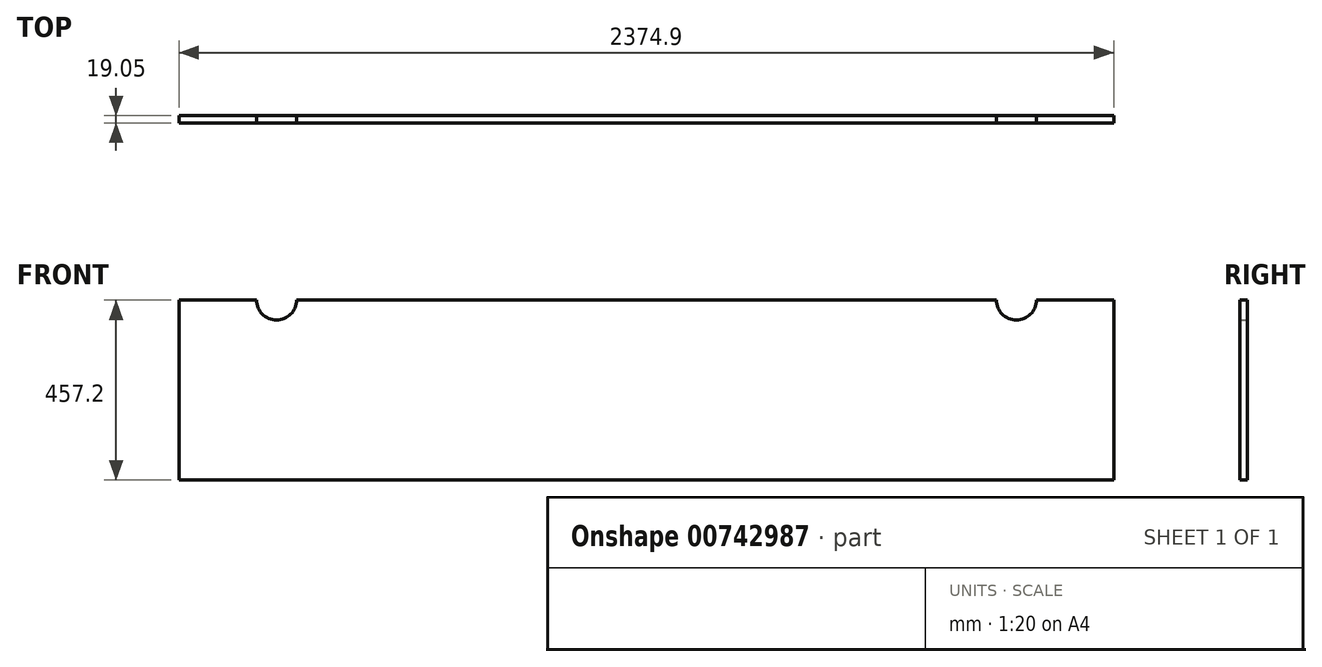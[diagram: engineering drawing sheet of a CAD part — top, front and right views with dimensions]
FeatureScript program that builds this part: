
annotation { "Feature Type Name" : "Feature", "Feature Type Description" : "" }
export const myFeature = defineFeature(function(context is Context, id is Id, definition is map)
    precondition{}
    {
        {
            var Q0;
            Q0=qCreatedBy(makeId("Front.planeOp"),FACE);
            var sketch = newSketch(context, id + "F0", { "sketchPlane" : qUnion([Q0])});
            skLineSegment(sketch, "E0.bottom", {"start": v(1187.45, 228.6) * mm, "end": v(-1187.45, 228.6) * mm});
            skLineSegment(sketch, "E0.top", {"start": v(1187.45, -228.6) * mm, "end": v(-1187.45, -228.6) * mm});
            skLineSegment(sketch, "E0.left", {"start": v(1187.45, 228.6) * mm, "end": v(1187.45, -228.6) * mm});
            skLineSegment(sketch, "E0.right", {"start": v(-1187.45, 228.6) * mm, "end": v(-1187.45, -228.6) * mm});
            skPoint(sketch, "E0.middle", {"position": v(0, 0) * mm});
            skLineSegment(sketch, "E1", {"start": v(-1187.45, 228.6) * mm, "end": v(-939.8, 228.6) * mm});
            skLineSegment(sketch, "E2", {"start": v(1187.45, 228.6) * mm, "end": v(939.8, 228.6) * mm});
            skCircle(sketch, "E3", {"center": v(-939.8, 228.6) * mm, "radius": 50.8 * mm});
            skCircle(sketch, "E4", {"center": v(939.8, 228.6) * mm, "radius": 50.8 * mm});
            skSolve(sketch);
        }
        {
            var Q0;
            Q0=makeQuery(id+"F0.imprint","IMPRINT",FACE,{"disambiguationData":[TD([[makeQuery(id+"F0.imprint","IMPRINT",EDGE,{"derivedFrom":sQuery(id+"F0.wireOp",EDGE,"E0.top")}),-1.0]])]});
            extrude(context, id + "F1", {"entities" : qUnion([Q0]), "depth" : 19.05 * mm, "offsetDistance" : 25.4 * mm});
        }
    });
